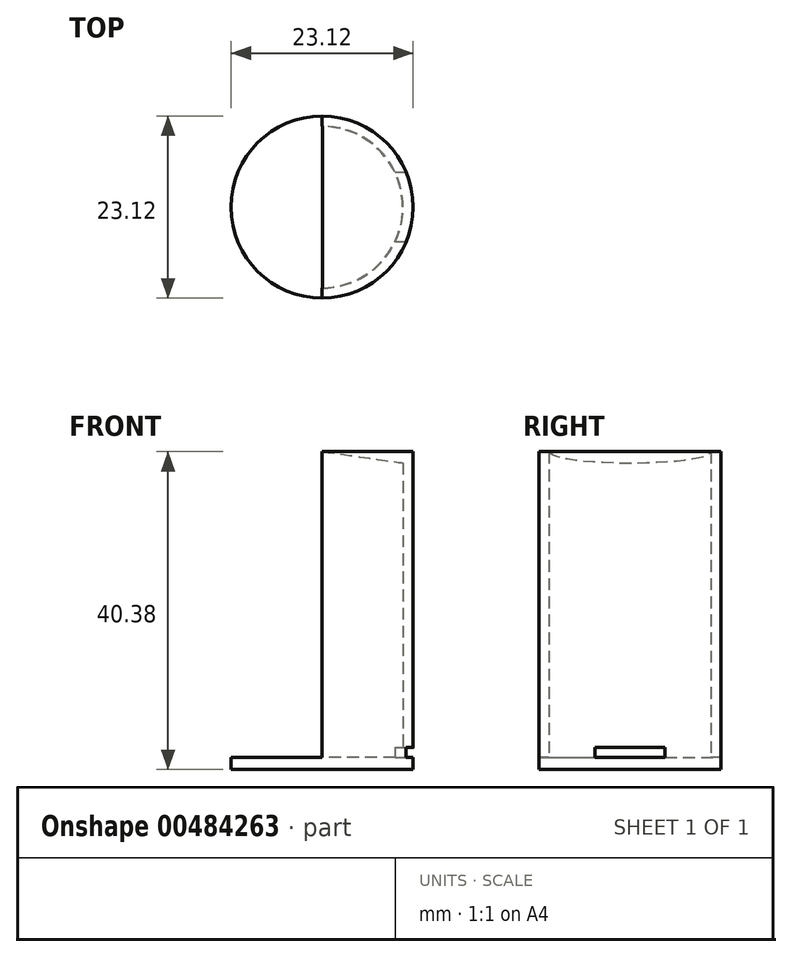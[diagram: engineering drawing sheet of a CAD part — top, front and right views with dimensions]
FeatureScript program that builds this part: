
annotation { "Feature Type Name" : "Feature", "Feature Type Description" : "" }
export const myFeature = defineFeature(function(context is Context, id is Id, definition is map)
    precondition{}
    {
        {
            var Q0;
            Q0=qCreatedBy(makeId("Top.planeOp"),FACE);
            var sketch = newSketch(context, id + "F0", { "sketchPlane" : qUnion([Q0])});
            skArc(sketch, "E0", {"start": v(0, -10.29) * mm, "mid": v(10.29, 0) * mm, "end": v(0, 10.29) * mm});
            skArc(sketch, "E1", {"start": v(0, -11.56) * mm, "mid": v(11.56, 0) * mm, "end": v(0, 11.56) * mm});
            skLineSegment(sketch, "E2", {"start": v(0, 11.56) * mm, "end": v(0, 10.29) * mm});
            skLineSegment(sketch, "E3.trimOffspring", {"start": v(0, -10.29) * mm, "end": v(0, -11.56) * mm});
            skSolve(sketch);
        }
        {
            var Q0;
            Q0 = qSketchRegion(id + "F0", true);
            extrude(context, id + "F1", {"entities" : qUnion([Q0]), "endBound" : BoundingType.SYMMETRIC, "depth" : 38.1 * mm});
        }
        {
            var Q0;
            Q0=makeQuery(id+"F1.opExtrude","CAP_FACE",FACE,{"disambiguationData":[OSD([sQuery(id+"F0.wireOp",EDGE,"E0"),sQuery(id+"F0.wireOp",EDGE,"E1"),sQuery(id+"F0.wireOp",EDGE,"E2"),sQuery(id+"F0.wireOp",EDGE,"E3.trimOffspring")])],"isStart":false});
            var sketch = newSketch(context, id + "F2", { "sketchPlane" : qUnion([Q0])});
            skArc(sketch, "E4", {"start": v(0, -11.56) * mm, "mid": v(11.56, 0) * mm, "end": v(0, 11.56) * mm});
            skLineSegment(sketch, "E5", {"start": v(0, 11.56) * mm, "end": v(0, -11.56) * mm});
            skSolve(sketch);
        }
        {
            var Q0;
            Q0 = qSketchRegion(id + "F2", true);
            extrude(context, id + "F3", {"entities" : qUnion([Q0]), "operationType" : NewBodyOperationType.ADD, "endBound" : BoundingType.SYMMETRIC, "depth" : 1.52 * mm});
        }
        {
            var Q0;
            Q0=makeQuery(id+"F3.opExtrude","CAP_EDGE",EDGE,{"disambiguationData":[OSD([sQuery(id+"F2.wireOp",EDGE,"E5")])],"isStart":true});
            chamfer(context, id + "F4", {"entities" : qUnion([Q0]), "chamferType" : ChamferType.OFFSET_ANGLE, "width" : 1.52 * mm, "oppositeDirection" : false, "angle" : 82 * degree, "tangentPropagation" : true});
        }
        {
            var Q0;
            Q0=makeQuery(id+"F1.opExtrude","CAP_FACE",FACE,{"disambiguationData":[OSD([sQuery(id+"F0.wireOp",EDGE,"E0"),sQuery(id+"F0.wireOp",EDGE,"E1"),sQuery(id+"F0.wireOp",EDGE,"E2"),sQuery(id+"F0.wireOp",EDGE,"E3.trimOffspring")])],"isStart":true});
            var sketch = newSketch(context, id + "F5", { "sketchPlane" : qUnion([Q0])});
            skCircle(sketch, "E6", {"center": v(0, 0) * mm, "radius": 11.56 * mm});
            skSolve(sketch);
        }
        {
            var Q0;
            Q0 = qSketchRegion(id + "F5", true);
            extrude(context, id + "F6", {"entities" : qUnion([Q0]), "operationType" : NewBodyOperationType.ADD, "depth" : 1.52 * mm});
        }
        {
            var Q0;
            Q0=makeQuery(id+"F6.opExtrude","CAP_FACE",FACE,{"disambiguationData":[OSD([sQuery(id+"F5.wireOp",EDGE,"E6")])],"isStart":true});
            var sketch = newSketch(context, id + "F7", { "sketchPlane" : qUnion([Q0])});
            skArc(sketch, "E7", {"start": v(10.67, -4.45) * mm, "mid": v(11.56, 0) * mm, "end": v(10.67, 4.45) * mm});
            skArc(sketch, "E8", {"start": v(9.28, -4.45) * mm, "mid": v(10.29, 0) * mm, "end": v(9.28, 4.44) * mm});
            skLineSegment(sketch, "E9", {"start": v(9.28, 4.45) * mm, "end": v(10.67, 4.45) * mm});
            skLineSegment(sketch, "E10", {"start": v(10.67, 4.45) * mm, "end": v(10.67, -4.45) * mm, "construction": true});
            skLineSegment(sketch, "E11", {"start": v(10.67, -4.44) * mm, "end": v(9.28, -4.45) * mm});
            skLineSegment(sketch, "E12", {"start": v(9.28, -4.45) * mm, "end": v(9.28, 4.45) * mm, "construction": true});
            skLineSegment(sketch, "E13", {"start": v(0, 0) * mm, "end": v(9.28, 0) * mm, "construction": true});
            skSolve(sketch);
        }
        {
            var Q0;
            Q0 = qSketchRegion(id + "F7", true);
            extrude(context, id + "F8", {"entities" : qUnion([Q0]), "operationType" : NewBodyOperationType.REMOVE, "depth" : 1.26 * mm});
        }
    });
